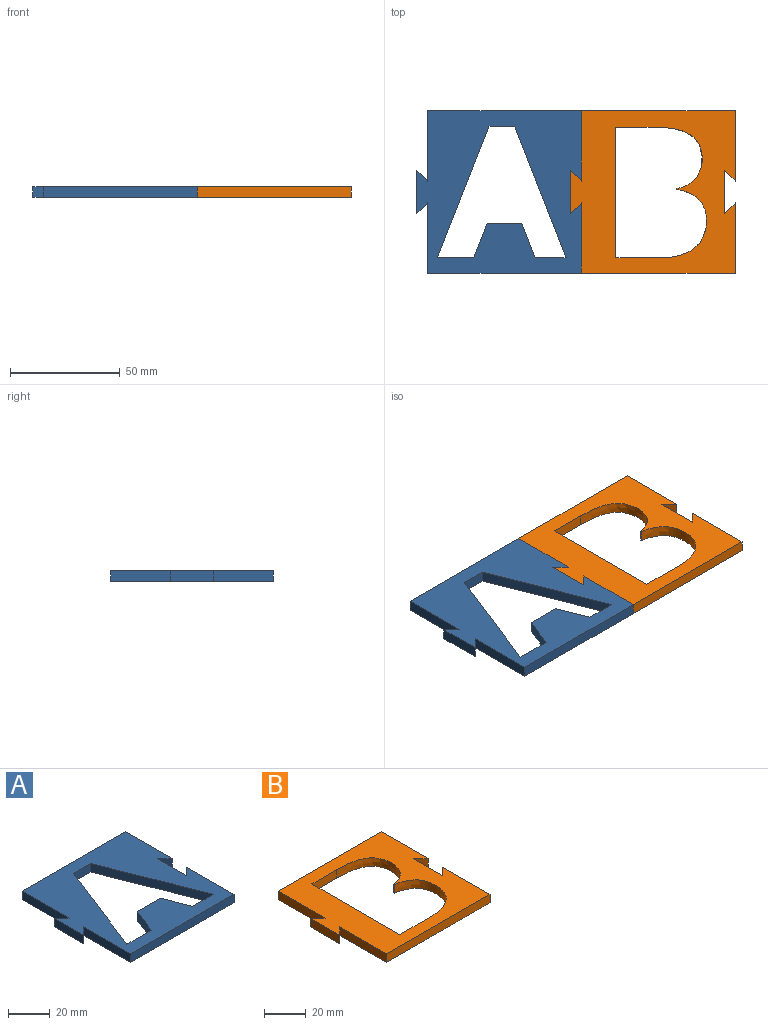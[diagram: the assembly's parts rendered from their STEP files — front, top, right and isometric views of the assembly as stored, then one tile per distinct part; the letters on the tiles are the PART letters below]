
ASSEMBLY  parts=2 mates=1
PART A: 22 faces, bbox 75x73.8x5 mm
  f0: plane 31.88x5mm, normal (-1,0,0), area 159.4mm2, adj f2,f14,f15,f21
  f1: plane 31.88x5mm, normal (1,0,0), area 159.4mm2, adj f2,f14,f15,f18
  f2: plane 75x73.77mm, normal (0,0,-1), area 3406.9mm2, adj f0,f1,f3,f4,f5,f6,f7,f8
  f3: plane 31.88x5mm, normal (1,0,0), area 159.4mm2, adj f2,f4,f15,f16
  f4: plane 70x5mm, normal (0,1,0), area 350mm2, adj f2,f3,f5,f15
  f5: plane 31.88x5mm, normal (-1,0,0), area 159.4mm2, adj f2,f4,f15,f19
  f6: plane 14.05x5mm, normal (0,1,0), area 70.2mm2, adj f2,f7,f13,f15
  f7: plane 15.77x6.16mm, normal (0.93,0.36,0), area 84.6mm2, adj f2,f6,f8,f15
  f8: plane 15.69x5mm, normal (0,1,0), area 78.5mm2, adj f2,f7,f9,f15
  f9: plane 15.77x6.11mm, normal (-0.93,0.36,0), area 84.6mm2, adj f2,f8,f10,f15
  f10: plane 16.59x5mm, normal (0,1,0), area 83mm2, adj f2,f9,f11,f15
  f11: plane 59.8x23.53mm, normal (0.93,-0.37,0), area 321.3mm2, adj f2,f10,f12,f15
  f12: plane 11.68x5mm, normal (0,-1,0), area 58.4mm2, adj f2,f11,f13,f15
  f13: plane 59.77x23.4mm, normal (-0.93,-0.36,0), area 321mm2, adj f2,f6,f12,f15
  f14: plane 70x5mm, normal (0,-1,0), area 350mm2, adj f0,f1,f2,f15
  f15: plane 75x73.77mm, normal (0,0,1), area 3406.9mm2, adj f0,f1,f3,f4,f5,f6,f7,f8
  f16: plane 5x5mm, normal (-0.71,-0.71,0), area 35.4mm2, adj f2,f3,f15,f17
  f17: plane 20x5mm, normal (1,0,0), area 100mm2, adj f2,f15,f16,f18
  f18: plane 5x5mm, normal (-0.71,0.71,0), area 35.4mm2, adj f1,f2,f15,f17
  f19: plane 5x5mm, normal (0.71,0.71,0), area 35.4mm2, adj f2,f5,f15,f20
  f20: plane 20x5mm, normal (-1,0,0), area 100mm2, adj f2,f15,f19,f21
  f21: plane 5x5mm, normal (0.71,-0.71,0), area 35.4mm2, adj f0,f2,f15,f20
PART B: 20 faces, bbox 75x73.8x5 mm
  f0: plane 20x5mm, normal (1,0,0), area 100mm2, adj f1,f17,f18,f19
  f1: plane 5x5mm, normal (-0.71,-0.71,0), area 35.4mm2, adj f0,f2,f18,f19
  f2: plane 31.88x5mm, normal (1,0,0), area 159.4mm2, adj f1,f3,f18,f19
  f3: plane 70x5mm, normal (0,1,0), area 350mm2, adj f2,f4,f18,f19
  f4: plane 31.88x5mm, normal (-1,0,0), area 159.4mm2, adj f3,f5,f18,f19
  f5: plane 5x5mm, normal (0.71,0.71,0), area 35.4mm2, adj f4,f6,f18,f19
  f6: plane 20x5mm, normal (-1,0,0), area 100mm2, adj f5,f7,f18,f19
  f7: plane 5x5mm, normal (0.71,-0.71,0), area 35.4mm2, adj f6,f8,f18,f19
  f8: plane 31.88x5mm, normal (-1,0,0), area 159.4mm2, adj f7,f9,f18,f19
  f9: plane 70x5mm, normal (0,-1,0), area 350mm2, adj f8,f10,f18,f19
  f10: plane 31.88x5mm, normal (1,0,0), area 159.4mm2, adj f9,f17,f18,f19
  f11: plane 21.56x5mm, normal (0,1,0), area 107.8mm2, adj f12,f16,f18,f19
  f12: plane 59.49x5mm, normal (1,0,0), area 297.5mm2, adj f11,f13,f18,f19
  f13: plane 16.86x5mm, normal (0,-1,0), area 84.3mm2, adj f12,f14,f18,f19
  f14: extruded ~27.93x22.42mm, area 250.4mm2, adj f13,f15,f18,f19
  f15: plane 5x0.41mm, normal (-1,0,0), area 2.1mm2, adj f14,f16,f18,f19
  f16: extruded ~31.16x19.65mm, area 257.3mm2, adj f11,f15,f18,f19
  f17: plane 5x5mm, normal (-0.71,0.71,0), area 35.4mm2, adj f0,f10,f18,f19
  f18: plane 75x73.77mm, normal (0,0,1), area 2962.5mm2, adj f0,f1,f2,f3,f4,f5,f6,f7
  f19: plane 75x73.77mm, normal (0,0,-1), area 2962.5mm2, adj f0,f1,f2,f3,f4,f5,f6,f7
PLACE A t=(-25.43,45.63,-28.31)mm
PLACE B t=(28.53,61.67,-28.31)mm
MATE fastened A.f3 <-> B.f4  axis (1,0,0) through (32.87,41.48,-25.81)mm
